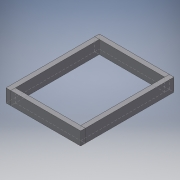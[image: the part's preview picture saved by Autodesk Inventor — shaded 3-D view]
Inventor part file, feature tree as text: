
AUTODESK INVENTOR PART (.ipt)
format: ipt  version: 2016 (Build 200138000, 138)  size: 156,672 bytes
history: native  units: in
note: dims shown in document units (in); Inventor stores cm internally (conversion verified against a paired STEP export)
features: sketch x6, split x4, extrude x2, boolean_combine x2
ambient origin geometry x8: Origin, YZ Plane, XZ Plane, XY Plane, X Axis, Y Axis, Z Axis, Center Point
bodies: Solid1 (feature_tree), Solid2 (feature_tree), Solid3 (feature_tree), Solid4 (feature_tree), Solid5 (feature_tree), Solid6 (feature_tree), Solid7 (feature_tree), Solid8 (feature_tree), Solid9 (feature_tree)
feature tree (14):
  extrude  "Extrusion1"  Depth=16.0in
  extrude  "Extrusion2"  Depth=18.0in
  split  "Split1"
  split  "Split2"
  split  "Split3"
  split  "Split4"
  boolean_combine  "Combine1"
  boolean_combine  "Combine2"
  sketch  "Sketch1"  dims[d0=20.0in d1=16.0in]
  sketch  "Sketch2"  dims[d2=2.8in d3=0.0in d4=18.0in]
  sketch  "Sketch3"  dims[d5=14.0in]
  sketch  "Sketch4"  dims[d7=2.8in d8=0.0in]
  sketch  "Sketch5"
  sketch  "Sketch6"
